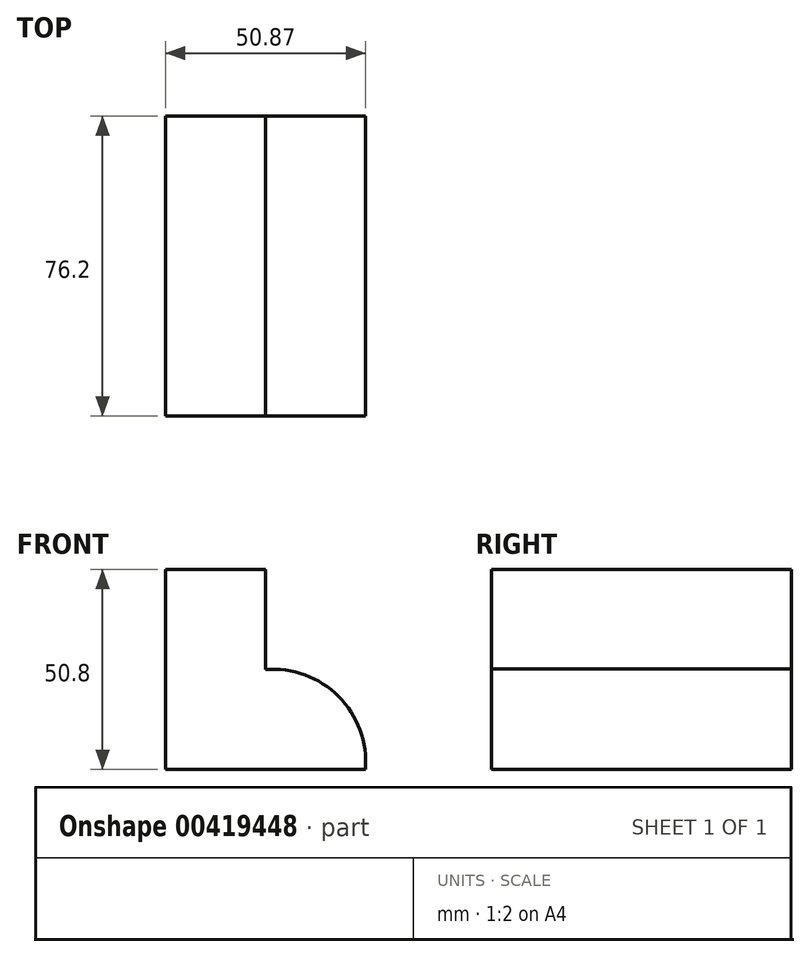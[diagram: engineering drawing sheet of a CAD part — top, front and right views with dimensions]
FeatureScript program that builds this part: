
annotation { "Feature Type Name" : "Feature", "Feature Type Description" : "" }
export const myFeature = defineFeature(function(context is Context, id is Id, definition is map)
    precondition{}
    {
        {
            var Q0;
            Q0=qCreatedBy(makeId("Front.planeOp"),FACE);
            var sketch = newSketch(context, id + "F0", { "sketchPlane" : qUnion([Q0])});
            skLineSegment(sketch, "E0", {"start": v(-45.64, 18.03) * mm, "end": v(-45.64, -32.77) * mm});
            skLineSegment(sketch, "E1", {"start": v(-45.64, -32.77) * mm, "end": v(5.16, -32.77) * mm});
            skLineSegment(sketch, "E2", {"start": v(-45.64, 18.03) * mm, "end": v(-20.24, 18.03) * mm});
            skLineSegment(sketch, "E3", {"start": v(-20.24, 18.03) * mm, "end": v(-20.24, -7.37) * mm});
            skArc(sketch, "E4", {"start": v(5.16, -32.77) * mm, "mid": v(-1.67, -14.2) * mm, "end": v(-20.24, -7.37) * mm});
            skSolve(sketch);
        }
        {
            var Q0;
            Q0=makeQuery(id+"F0.imprint","IMPRINT",FACE,{"disambiguationData":[TD([[makeQuery(id+"F0.imprint","IMPRINT",EDGE,{"derivedFrom":sQuery(id+"F0.wireOp",EDGE,"E0")}),1.0]])]});
            extrude(context, id + "F1", {"entities" : qUnion([Q0]), "depth" : 76.2 * mm});
        }
    });
